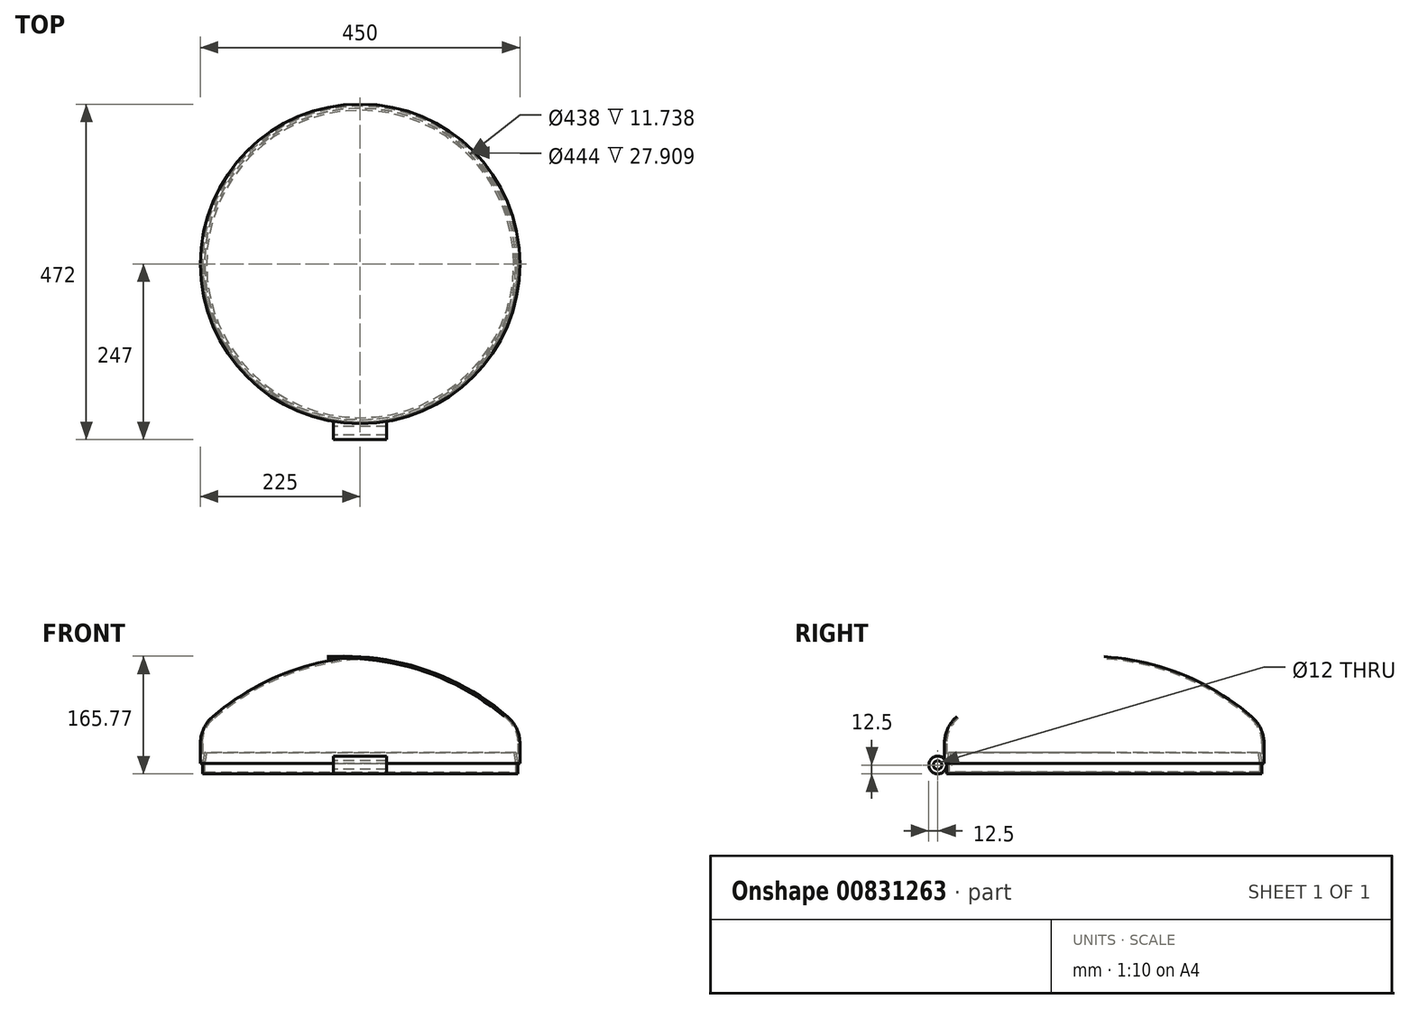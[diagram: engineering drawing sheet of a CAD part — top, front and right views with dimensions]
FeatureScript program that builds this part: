
annotation { "Feature Type Name" : "Feature", "Feature Type Description" : "" }
export const myFeature = defineFeature(function(context is Context, id is Id, definition is map)
    precondition{}
    {
        {
            var Q0;
            Q0=qCreatedBy(makeId("Front.planeOp"),FACE);
            var sketch = newSketch(context, id + "F0", { "sketchPlane" : qUnion([Q0])});
            skLineSegment(sketch, "E0.bottom", {"start": v(225, 150) * mm, "end": v(-225, 150) * mm, "construction": true});
            skLineSegment(sketch, "E0.top", {"start": v(225, -150) * mm, "end": v(-225, -150) * mm, "construction": true});
            skLineSegment(sketch, "E0.left", {"start": v(225, 150) * mm, "end": v(225, -150) * mm, "construction": true});
            skLineSegment(sketch, "E0.right", {"start": v(-225, 150) * mm, "end": v(-225, -150) * mm, "construction": true});
            skPoint(sketch, "E0.middle", {"position": v(0, 0) * mm});
            skLineSegment(sketch, "E1", {"start": v(-225, 0) * mm, "end": v(225, 0) * mm, "construction": true});
            skLineSegment(sketch, "E2", {"start": v(-225, 100) * mm, "end": v(225, 100) * mm, "construction": true});
            skLineSegment(sketch, "E3", {"start": v(-225, 50) * mm, "end": v(225, 50) * mm, "construction": true});
            skLineSegment(sketch, "E4", {"start": v(-89.19, 50) * mm, "end": v(-89.19, 50) * mm});
            skLineSegment(sketch, "E5", {"start": v(0, 0) * mm, "end": v(0, 150) * mm, "construction": true});
            skArc(sketch, "E6.trimOffspring", {"start": v(0, 150) * mm, "mid": v(-121.4, 120.05) * mm, "end": v(-225, 50) * mm});
            skLineSegment(sketch, "E7", {"start": v(-225, 50) * mm, "end": v(-225, 0) * mm});
            skLineSegment(sketch, "E8", {"start": v(0, 150) * mm, "end": v(0, 0) * mm});
            skLineSegment(sketch, "E9", {"start": v(-225, 0) * mm, "end": v(0, 0) * mm});
            skSolve(sketch);
        }
        {
            var Q0;
            Q0 = qSketchRegion(id + "F0", true);
            var Q1;
            Q1=sQuery(id+"F0.wireOp",EDGE,"E6.trimOffspring");
            var Q2;
            Q2=sQuery(id+"F0.wireOp",EDGE,"E5");
            revolve(context, id + "F1", {"surfaceOperationType" : NewSurfaceOperationType.NEW, "entities" : qUnion([Q0]), "surfaceEntities" : qUnion([Q1]), "axis" : qUnion([Q2]), "revolveType" : RevolveType.FULL});
        }
        {
            var Q0;
            Q0=makeQuery(id+"F1.opRevolve","SWEPT_EDGE",EDGE,{"disambiguationData":[OSD([sQuery(id+"F0.wireOp",EDGE,"E6.trimOffspring"),sQuery(id+"F0.wireOp",EDGE,"E7")])]});
            fillet(context, id + "F2", {"entities" : qUnion([Q0]), "radius" : 50 * mm, "tangentPropagation" : true, "allowEdgeOverflow" : false});
        }
        {
            var Q0;
            Q0=makeQuery(id+"F1.opRevolve","SWEPT_FACE",FACE,{"disambiguationData":[OSD([sQuery(id+"F0.wireOp",EDGE,"E9")])]});
            shell(context, id + "F3", {"entities" : qUnion([Q0]), "thickness" : 3 * mm});
        }
        {
            var Q0;
            Q0=makeQuery(id+"F1.opRevolve","SWEPT_FACE",FACE,{"disambiguationData":[OSD([sQuery(id+"F0.wireOp",EDGE,"E9")])]});
            var sketch = newSketch(context, id + "F4", { "sketchPlane" : qUnion([Q0])});
            skCircle(sketch, "E10.0", {"center": v(0, 0) * mm, "radius": 222 * mm});
            skSolve(sketch);
        }
        {
            var Q0;
            Q0 = qSketchRegion(id + "F4", true);
            extrude(context, id + "F5", {"entities" : qUnion([Q0]), "oppositeDirection" : true, "depth" : 15 * mm, "offsetDistance" : 25 * mm, "hasDraft" : true, "draftAngle" : 10 * degree, "draftPullDirection" : true, "hasSecondDirection" : true, "secondDirectionOppositeDirection" : false, "secondDirectionDepth" : 15 * mm});
        }
        {
            var Q0;
            Q0=makeQuery(id+"F5.opExtrude","CAP_FACE",FACE,{"disambiguationData":[OSD([sQuery(id+"F4.wireOp",EDGE,"E10.0")])],"isStart":false});
            shell(context, id + "F6", {"entities" : qUnion([Q0]), "thickness" : 3 * mm});
        }
        {
            var Q0;
            Q0=qCreatedBy(makeId("Right.planeOp"),FACE);
            var sketch = newSketch(context, id + "F7", { "sketchPlane" : qUnion([Q0])});
            skCircle(sketch, "E11", {"center": v(-234.5, -2.5) * mm, "radius": 12.5 * mm});
            skLineSegment(sketch, "E12", {"start": v(-222, -15) * mm, "end": v(-222, 0) * mm});
            skLineSegment(sketch, "E13", {"start": v(222, 0) * mm, "end": v(222, -15) * mm});
            skLineSegment(sketch, "E14", {"start": v(-222, -15) * mm, "end": v(-222, 67.4) * mm, "construction": true});
            skCircle(sketch, "E15", {"center": v(-234.5, -2.5) * mm, "radius": 6 * mm});
            skSolve(sketch);
        }
        {
            var Q0;
            Q0=makeQuery(id+"F7.imprint","IMPRINT",FACE,{"disambiguationData":[TD([[makeQuery(id+"F7.imprint","IMPRINT",EDGE,{"derivedFrom":sQuery(id+"F7.wireOp",EDGE,"E11")}),1.0]])]});
            extrude(context, id + "F8", {"entities" : qUnion([Q0]), "endBound" : BoundingType.SYMMETRIC, "depth" : 75 * mm, "offsetDistance" : 25 * mm});
        }
    });
